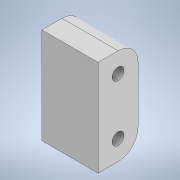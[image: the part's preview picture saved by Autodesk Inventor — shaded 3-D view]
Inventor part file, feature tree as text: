
AUTODESK INVENTOR PART (.ipt)
format: ipt  version: 2021 (Build 250183000, 183)  size: 169,472 bytes
history: native  units: mm
features: extrude x8, sketch x7, projected_geometry x4
ambient origin geometry x8: Origin, YZ Plane, XZ Plane, XY Plane, X Axis, Y Axis, Z Axis, Center Point
bodies: Solid1 (feature_tree)
feature tree (19):
  extrude  "Extrusion1"  Depth=40.0mm
  extrude  "Extrusion2"  Depth=8.5mm
  sketch  "Sketch3"  dims[d4=22.5mm d5=28.5mm]
  extrude  "Extrusion3"  Depth=28.5mm
  extrude  "Extrusion4"  Depth=28.5mm TaperAngle=0.0deg
  extrude  "Extrusion5"  Depth=3.0mm TaperAngle=0.0deg
  extrude  "Extrusion8"  Depth=3.0mm TaperAngle=0.0deg
  extrude  "Extrusion9"  Depth=10.0mm
  extrude  "Extrusion10"  Depth=10.0mm TaperAngle=0.0deg
  sketch  "Sketch1"  dims[d0=40.0mm d1=8.5mm]
  sketch  "Sketch2"  dims[d2=22.5mm d3=8.5mm]
  sketch  "Sketch4"  dims[d6=28.5mm d7=3.0mm d8=0.0mm]
  sketch  "Sketch7"  dims[d9=34.0mm d10=3.0mm d11=0.0mm]
  sketch  "Sketch8"  dims[d12=3.0mm d13=0.0mm d14=3.0mm d15=0.0mm]
  projected_geometry  "Projected Loop5"
  projected_geometry  "Projected Loop6"
  sketch  "Sketch9"  dims[d16=8.5mm d17=8.5mm d18=3.0mm d19=0.0mm d24=10.0mm d25=0.0mm d26=10.0mm d27=0.0mm d28=10.0mm d29=0.0mm d20=0.5mm d21=0.872665mm d22=0.5mm d23=0.872665mm]
  projected_geometry  "Projected Loop7"
  projected_geometry  "Projected Loop8"
